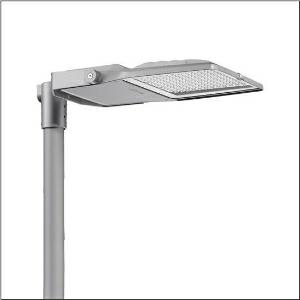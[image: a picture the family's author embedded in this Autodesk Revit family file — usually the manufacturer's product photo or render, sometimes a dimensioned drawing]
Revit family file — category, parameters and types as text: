
# Revit family: floodlight_fl_21_midi___pl61_5xa7782e4c3a_e87b
name_source: partatom
category: Lighting Fixtures
units: mm (PartAtom-declared; Revit-internal decimal feet)

## family parameters
Cut with Voids When Loaded = No
Host = Face
Light Source = No
Part Type = Normal
Room Calculation Point = No
Round Connector Dimension = Use Diameter
Shared = No

## types (1)
- --- (1 x LED, 27490 lm, 208.1 W, 4000K)
    Apparent Load = 208 VA
    CIE Flux Codes = 33 65 98 100 100
    Color Rendering = 70
    Color Temperature = 4000K
    Default Elevation = 1800 mm
    Description = Floodlight FL 21 midi, floodlight, primary light control with lens, of PMMA, primary optical cover: protective disc, of toughened safety glass, transparent, light distribution: PL61, light emission: direct distribution, installation type: surface-mounted, LED, High Power LED, rated luminous flux: 27.490lm, luminous efficacy: 132lm/W, light colour: 740, colour temperature: 4000K, control gear: ECG iQ, control: optimised constant luminous flux control (CLO 2.0), Desk-Remote (wireless, voltage-free reading and setting of iQ features in the workshop via application-optimized NFC function/RFID function), Smart-Wire, Night-Set, Temp-Guard, Auto-Match, Street-Remote, with terminal, 6-pole, mains connection: 220..240V, AC, 50/60Hz, start of lifetime: 208W, end of lifetime: 227W, reduction: 90W, luminaire housing, of diecast aluminium, powder-coated, Siteco® metallic grey (DB 702S), corrosivity category C5 according to DIN EN ISO 12944, mast bracket, of steel, galvanised, powder-coated, Siteco® metallic grey (DB 702S), protection rating (complete): IP66, insulation class (complete): insulation class II (safety insulation), certification: CE, protection symbol: D, impact resistance: IK08, permissible operating ambient temperature: -40..+40°C, permissible operating ambient temperature for outdoor applications: -40..+50°C, standard: DIN EN 12944, packaging unit: 1 piece

Light Distribution: PL61
    Height = 76 mm
    Lamp = 1 x LED
    Lamp Light Flux = 27490 lm
    Lamp Power = 208.1 W
    Lamp count = 1
    Length = 657 mm
    Luminous efficacy = 132 lm/W
    Manufacturer = Siteco
    ModVariant = No
    Model = 5XA7782E4C3A
    Number of Poles = 1
    OnlyDefault = Yes
    Power Factor = 1
    Product Name = Floodlight FL 21 midi | PL61
    Product group = floodlight | pylon top
    ProductGroupID = 6101
    Protection Class = Protection class II
    Protection Degree = IP 66
    RLX_Detail_Level = 1
    RlxData = <blob elided: 153545 chars, md5=76ef8062>
    Socket = socket
    Standby Power = 0 W
    System Light Flux = 27490 lm
    System Power = 208 W
    Type Comments = factory setting: luminous flux: 100 % | dim-lin: 254 | 710 mA
    Type Image = l_1007123.jpg
    URL = http://relux.com
    VarID = @adj_017113
    Voltage = 0 V
    Weight = 0.00 kg
    Width = 442 mm

## geometry (parser evidence)
native form markers: Blend x4, Sweep x13
no freeform markers — native parametric forms only
